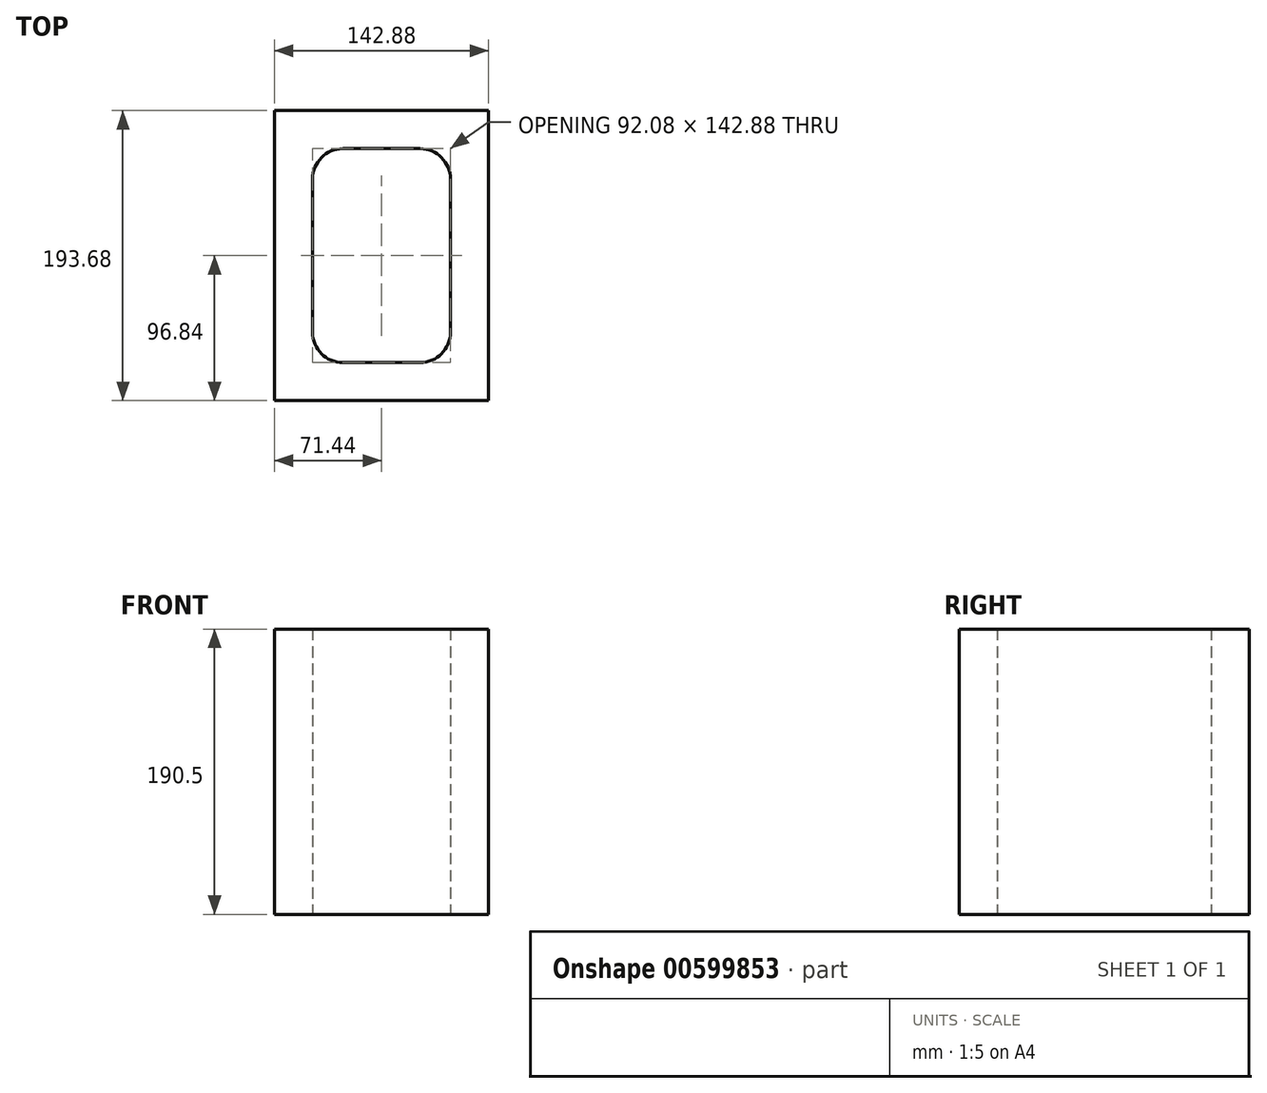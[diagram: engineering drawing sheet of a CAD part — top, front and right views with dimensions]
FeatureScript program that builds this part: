
annotation { "Feature Type Name" : "Feature", "Feature Type Description" : "" }
export const myFeature = defineFeature(function(context is Context, id is Id, definition is map)
    precondition{}
    {
        {
            var Q0;
            Q0=qCreatedBy(makeId("Top.planeOp"),FACE);
            var sketch = newSketch(context, id + "F0", { "sketchPlane" : qUnion([Q0])});
            skLineSegment(sketch, "E0.bottom", {"start": v(71.44, 96.84) * mm, "end": v(-71.44, 96.84) * mm});
            skLineSegment(sketch, "E0.top", {"start": v(71.44, -96.84) * mm, "end": v(-71.44, -96.84) * mm});
            skLineSegment(sketch, "E0.left", {"start": v(71.44, 96.84) * mm, "end": v(71.44, -96.84) * mm});
            skLineSegment(sketch, "E0.right", {"start": v(-71.44, 96.84) * mm, "end": v(-71.44, -96.84) * mm});
            skPoint(sketch, "E0.middle", {"position": v(0, 0) * mm});
            skLineSegment(sketch, "E1.top", {"start": v(25.72, 71.44) * mm, "end": v(-25.72, 71.44) * mm});
            skLineSegment(sketch, "E1.left", {"start": v(46.04, 0) * mm, "end": v(46.04, 51.12) * mm});
            skLineSegment(sketch, "E1.right", {"start": v(-46.04, 0) * mm, "end": v(-46.04, 51.12) * mm});
            skPoint(sketch, "E1.middle", {"position": v(0, 92.08) * mm});
            skLineSegment(sketch, "E2", {"start": v(-132.31, 0) * mm, "end": v(174.12, 0) * mm, "construction": true});
            skPoint(sketch, "E2.endSnap0", {"position": v(71.44, 0) * mm});
            skPoint(sketch, "E3.visualSharp", {"position": v(-46.04, 71.44) * mm});
            skArc(sketch, "E3.filletArc", {"start": v(-25.72, 71.44) * mm, "mid": v(-40.09, 65.49) * mm, "end": v(-46.04, 51.12) * mm});
            skPoint(sketch, "E4.visualSharp", {"position": v(46.04, 71.44) * mm});
            skArc(sketch, "E4.filletArc", {"start": v(46.04, 51.12) * mm, "mid": v(40.09, 65.49) * mm, "end": v(25.72, 71.44) * mm});
            skPoint(sketch, "E5.MirrorP", {"position": v(46.04, -71.44) * mm});
            skArc(sketch, "E6.MirrorCS", {"start": v(46.04, -51.12) * mm, "mid": v(40.09, -65.49) * mm, "end": v(25.72, -71.44) * mm});
            skArc(sketch, "E7.MirrorCS", {"start": v(-25.72, -71.44) * mm, "mid": v(-40.09, -65.49) * mm, "end": v(-46.04, -51.12) * mm});
            skLineSegment(sketch, "E8.MirrorCS", {"start": v(25.72, -71.44) * mm, "end": v(-25.72, -71.44) * mm});
            skLineSegment(sketch, "E9.MirrorCS", {"start": v(46.04, 0) * mm, "end": v(46.04, -51.12) * mm});
            skLineSegment(sketch, "E10.MirrorCS", {"start": v(-46.04, 0) * mm, "end": v(-46.04, -51.12) * mm});
            skPoint(sketch, "E11.MirrorP", {"position": v(-46.04, -71.44) * mm});
            skLineSegment(sketch, "E12", {"start": v(0, 177.27) * mm, "end": v(0, -155.84) * mm, "construction": true});
            skSolve(sketch);
        }
        {
            var Q0;
            Q0=makeQuery(id+"F0.imprint","IMPRINT",FACE,{"disambiguationData":[TD([[makeQuery(id+"F0.imprint","IMPRINT",EDGE,{"derivedFrom":sQuery(id+"F0.wireOp",EDGE,"E0.bottom")}),1.0]])]});
            extrude(context, id + "F1", {"entities" : qUnion([Q0]), "endBound" : BoundingType.SYMMETRIC, "depth" : 190.5 * mm, "offsetDistance" : 25.4 * mm});
        }
    });
